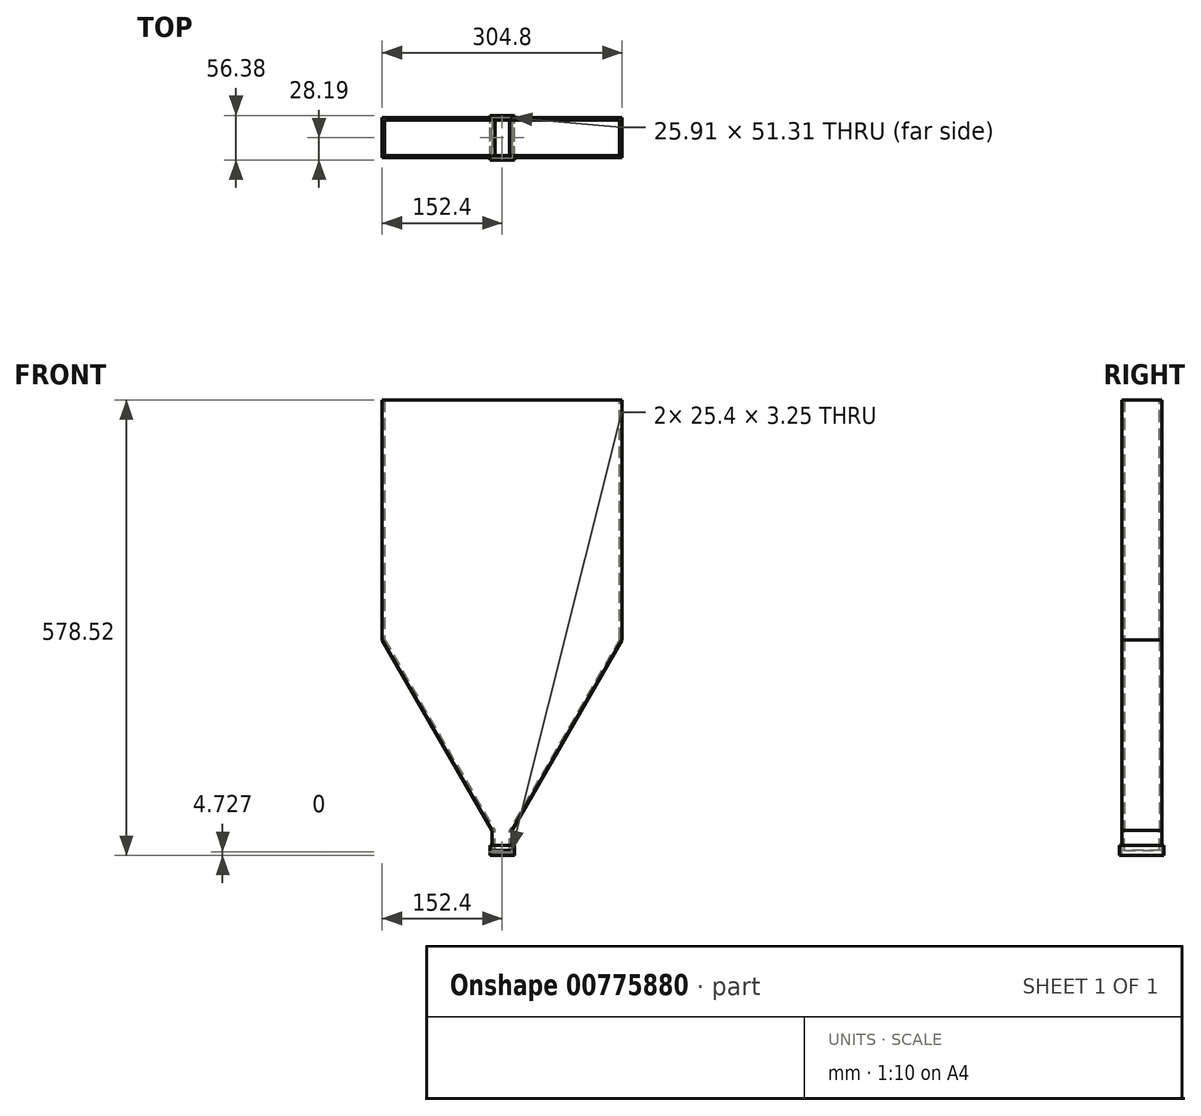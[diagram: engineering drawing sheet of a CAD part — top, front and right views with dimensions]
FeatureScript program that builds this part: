
annotation { "Feature Type Name" : "Feature", "Feature Type Description" : "" }
export const myFeature = defineFeature(function(context is Context, id is Id, definition is map)
    precondition{}
    {
        {
            var Q0;
            Q0=qCreatedBy(makeId("Front.planeOp"),FACE);
            var sketch = newSketch(context, id + "F0", { "sketchPlane" : qUnion([Q0])});
            skLineSegment(sketch, "E0", {"start": v(0, 0) * mm, "end": v(152.4, 0) * mm, "construction": true});
            skLineSegment(sketch, "E1", {"start": v(152.4, 0) * mm, "end": v(152.4, 304.8) * mm});
            skLineSegment(sketch, "E2", {"start": v(152.4, 304.8) * mm, "end": v(-152.4, 304.8) * mm});
            skLineSegment(sketch, "E3", {"start": v(-152.4, 304.8) * mm, "end": v(-152.4, 0) * mm});
            skLineSegment(sketch, "E4", {"start": v(-152.4, 0) * mm, "end": v(0, 0) * mm, "construction": true});
            skLineSegment(sketch, "E5", {"start": v(-152.4, 0) * mm, "end": v(0, -263.96) * mm});
            skLineSegment(sketch, "E6", {"start": v(152.4, 0) * mm, "end": v(0, -263.96) * mm});
            skLineSegment(sketch, "E7", {"start": v(0, 0) * mm, "end": v(0, -263.96) * mm, "construction": true});
            skLineSegment(sketch, "E8", {"start": v(0, -263.96) * mm, "end": v(0, -241.97) * mm, "construction": true});
            skLineSegment(sketch, "E9", {"start": v(-12.7, -241.97) * mm, "end": v(12.7, -241.97) * mm});
            skSolve(sketch);
        }
        {
            var Q0;
            {var subQ3=sQuery(id+"F0.wireOp",EDGE,"E1");Q0=makeQuery(id+"F0.imprint","IMPRINT",FACE,{"disambiguationData":[TD([[makeQuery(id+"F0.imprint","IMPRINT",EDGE,{"derivedFrom":subQ3}),1.0]])]});}
            var Q1;
            {var subQ3=sQuery(id+"F0.wireOp",EDGE,"E9");Q1=makeQuery(id+"F0.imprint","IMPRINT",FACE,{"disambiguationData":[TD([[makeQuery(id+"F0.imprint","IMPRINT",EDGE,{"derivedFrom":subQ3}),-1.0]])]});}
            extrude(context, id + "F1", {"entities" : qUnion([Q0, Q1]), "depth" : 25.4 * mm, "offsetDistance" : 25.4 * mm, "hasSecondDirection" : true, "secondDirectionOppositeDirection" : true, "secondDirectionDepth" : 25.4 * mm});
        }
        {
            var Q0;
            Q0=makeQuery(id+"F1.opExtrude","SWEPT_FACE",FACE,{"disambiguationData":[OSD([sQuery(id+"F0.wireOp",EDGE,"E2")])]});
            shell(context, id + "F2", {"entities" : qUnion([Q0]), "thickness" : 3 * mm});
        }
        {
            var Q0;
            {var subQ3=sQuery(id+"F0.wireOp",EDGE,"E9");Q0=makeQuery(id+"F0.imprint","IMPRINT",FACE,{"disambiguationData":[TD([[makeQuery(id+"F0.imprint","IMPRINT",EDGE,{"derivedFrom":subQ3}),-1.0]])]});}
            extrude(context, id + "F3", {"entities" : qUnion([Q0]), "operationType" : NewBodyOperationType.REMOVE, "oppositeDirection" : true, "depth" : 25.4 * mm, "offsetDistance" : 25.4 * mm, "hasSecondDirection" : true, "secondDirectionOppositeDirection" : false, "secondDirectionDepth" : 25.4 * mm});
        }
        {
            var Q0;
            Q0=makeQuery(id+"F3.boolean.opBoolean","COPY",FACE,{"derivedFrom":makeQuery(id+"F3.opExtrude","SWEPT_FACE",FACE,{"disambiguationData":[OSD([sQuery(id+"F0.wireOp",EDGE,"E9")])]})});
            extrude(context, id + "F4", {"entities" : qUnion([Q0]), "operationType" : NewBodyOperationType.ADD, "depth" : 25.4 * mm, "offsetDistance" : 25.4 * mm});
        }
        {
            var Q0;
            Q0=makeQuery(id+"F4.opExtrude","CAP_FACE",FACE,{"disambiguationData":[OSD([sQuery(id+"F0.wireOp",EDGE,"E9")])],"isStart":false});
            var sketch = newSketch(context, id + "F5", { "sketchPlane" : qUnion([Q0])});
            skLineSegment(sketch, "E10.bottom", {"start": v(12.95, 25.65) * mm, "end": v(-12.95, 25.65) * mm});
            skLineSegment(sketch, "E10.top", {"start": v(12.95, -25.65) * mm, "end": v(-12.95, -25.65) * mm});
            skLineSegment(sketch, "E10.left", {"start": v(12.95, 25.65) * mm, "end": v(12.95, -25.65) * mm});
            skLineSegment(sketch, "E10.right", {"start": v(-12.95, 25.65) * mm, "end": v(-12.95, -25.65) * mm});
            skPoint(sketch, "E10.middle", {"position": v(0, 0) * mm});
            skLineSegment(sketch, "E11", {"start": v(0, 25.4) * mm, "end": v(0, 25.65) * mm, "construction": true});
            skLineSegment(sketch, "E12", {"start": v(12.7, 0) * mm, "end": v(12.95, 0) * mm, "construction": true});
            skLineSegment(sketch, "E13.bottom", {"start": v(15.5, 28.2) * mm, "end": v(-15.5, 28.2) * mm});
            skLineSegment(sketch, "E13.top", {"start": v(15.5, -28.2) * mm, "end": v(-15.5, -28.2) * mm});
            skLineSegment(sketch, "E13.left", {"start": v(15.5, 28.2) * mm, "end": v(15.5, -28.2) * mm});
            skLineSegment(sketch, "E13.right", {"start": v(-15.5, 28.2) * mm, "end": v(-15.5, -28.2) * mm});
            skLineSegment(sketch, "E14", {"start": v(0, 25.65) * mm, "end": v(0, 28.2) * mm, "construction": true});
            skLineSegment(sketch, "E15", {"start": v(12.95, 0) * mm, "end": v(15.5, 0) * mm, "construction": true});
            skSolve(sketch);
        }
        {
            var Q0;
            Q0 = qSketchRegion(id + "F5", true);
            extrude(context, id + "F6", {"entities" : qUnion([Q0]), "oppositeDirection" : true, "depth" : 6.35 * mm, "offsetDistance" : 25.4 * mm, "hasSecondDirection" : true, "secondDirectionOppositeDirection" : false, "secondDirectionDepth" : 6.35 * mm});
        }
        {
            var Q0;
            Q0=makeQuery(id+"F6.opExtrude","SWEPT_FACE",FACE,{"disambiguationData":[OSD([sQuery(id+"F5.wireOp",EDGE,"E13.bottom")])]});
            var sketch = newSketch(context, id + "F7", { "sketchPlane" : qUnion([Q0])});
            skLineSegment(sketch, "E16", {"start": v(0, -261.02) * mm, "end": v(0, -273.72) * mm, "construction": true});
            skLineSegment(sketch, "E17", {"start": v(-15.5, -267.37) * mm, "end": v(15.5, -267.37) * mm, "construction": true});
            skLineSegment(sketch, "E18", {"start": v(0, -267.37) * mm, "end": v(0, -269) * mm, "construction": true});
            skLineSegment(sketch, "E19.bottom", {"start": v(12.7, -267.37) * mm, "end": v(-12.7, -267.37) * mm});
            skLineSegment(sketch, "E19.top", {"start": v(12.7, -270.62) * mm, "end": v(-12.7, -270.62) * mm});
            skLineSegment(sketch, "E19.left", {"start": v(12.7, -267.37) * mm, "end": v(12.7, -270.62) * mm});
            skLineSegment(sketch, "E19.right", {"start": v(-12.7, -267.37) * mm, "end": v(-12.7, -270.62) * mm});
            skPoint(sketch, "E19.middle", {"position": v(0, -269) * mm});
            skSolve(sketch);
        }
        {
            var Q0;
            Q0=makeQuery(id+"F7.imprint","IMPRINT",FACE,{"disambiguationData":[TD([[makeQuery(id+"F7.imprint","IMPRINT",EDGE,{"derivedFrom":sQuery(id+"F7.wireOp",EDGE,"E19.bottom")}),1.0]])]});
            extrude(context, id + "F8", {"entities" : qUnion([Q0]), "operationType" : NewBodyOperationType.REMOVE, "oppositeDirection" : true, "depth" : 76.2 * mm, "offsetDistance" : 25.4 * mm});
        }
    });
